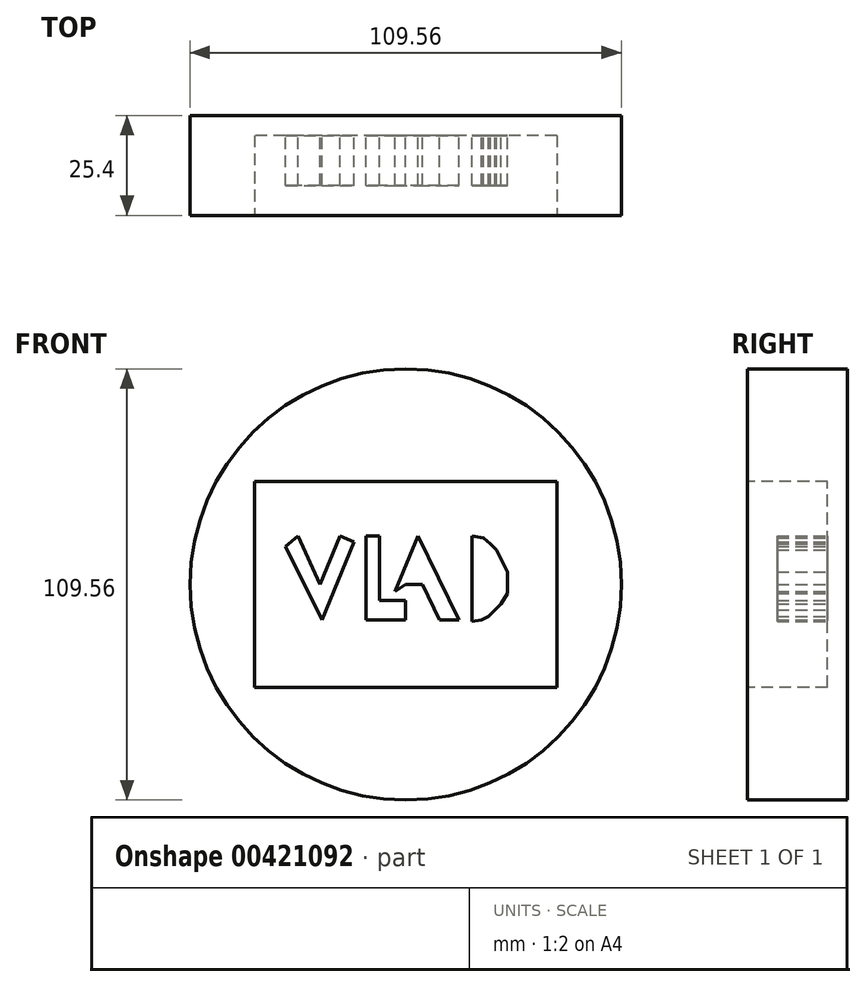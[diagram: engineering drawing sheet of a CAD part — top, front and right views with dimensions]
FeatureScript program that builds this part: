
annotation { "Feature Type Name" : "Feature", "Feature Type Description" : "" }
export const myFeature = defineFeature(function(context is Context, id is Id, definition is map)
    precondition{}
    {
        {
            var Q0;
            Q0=qCreatedBy(makeId("Front.planeOp"),FACE);
            var sketch = newSketch(context, id + "F0", { "sketchPlane" : qUnion([Q0])});
            skCircle(sketch, "E0", {"center": v(0, 0) * mm, "radius": 54.78 * mm});
            skSolve(sketch);
        }
        {
            var Q0;
            Q0 = qSketchRegion(id + "F0", true);
            extrude(context, id + "F1", {"entities" : qUnion([Q0]), "depth" : 25.4 * mm});
        }
        {
            var Q0;
            Q0=makeQuery(id+"F1.opExtrude","CAP_FACE",FACE,{"disambiguationData":[OSD([sQuery(id+"F0.wireOp",EDGE,"E0")])],"isStart":false});
            var sketch = newSketch(context, id + "F2", { "sketchPlane" : qUnion([Q0])});
            skLineSegment(sketch, "E1.bottom", {"start": v(38.38, -26.15) * mm, "end": v(-38.38, -26.15) * mm});
            skLineSegment(sketch, "E1.top", {"start": v(38.38, 26.15) * mm, "end": v(-38.38, 26.15) * mm});
            skLineSegment(sketch, "E1.left", {"start": v(38.38, -26.15) * mm, "end": v(38.38, 26.15) * mm});
            skLineSegment(sketch, "E1.right", {"start": v(-38.38, -26.15) * mm, "end": v(-38.38, 26.15) * mm});
            skPoint(sketch, "E1.middle", {"position": v(0, 0) * mm});
            skSolve(sketch);
        }
        {
            var Q0;
            Q0=makeQuery(id+"F2.imprint","IMPRINT",FACE,{"disambiguationData":[TD([[makeQuery(id+"F2.imprint","IMPRINT",EDGE,{"derivedFrom":sQuery(id+"F2.wireOp",EDGE,"E1.bottom")}),-1.0]])]});
            extrude(context, id + "F3", {"entities" : qUnion([Q0]), "operationType" : NewBodyOperationType.REMOVE, "oppositeDirection" : true, "depth" : 20.32 * mm});
        }
        {
            var Q0;
            Q0=makeQuery(id+"F3.boolean.opBoolean","COPY",FACE,{"derivedFrom":makeQuery(id+"F3.opExtrude","CAP_FACE",FACE,{"disambiguationData":[OSD([sQuery(id+"F2.wireOp",EDGE,"E1.bottom"),sQuery(id+"F2.wireOp",EDGE,"E1.top"),sQuery(id+"F2.wireOp",EDGE,"E1.left"),sQuery(id+"F2.wireOp",EDGE,"E1.right")])],"isStart":false})});
            var sketch = newSketch(context, id + "F4", { "sketchPlane" : qUnion([Q0])});
            skLineSegment(sketch, "E2", {"start": v(-30.48, 9.68) * mm, "end": v(-21.32, -8.96) * mm});
            skLineSegment(sketch, "E3", {"start": v(-21.32, -8.96) * mm, "end": v(-13.15, 10.82) * mm});
            skLineSegment(sketch, "E4", {"start": v(-13.15, 10.82) * mm, "end": v(-16.73, 12.3) * mm});
            skLineSegment(sketch, "E5", {"start": v(-16.73, 12.3) * mm, "end": v(-21.81, 0) * mm});
            skLineSegment(sketch, "E6", {"start": v(-21.81, 0) * mm, "end": v(-27.37, 12.3) * mm});
            skLineSegment(sketch, "E7", {"start": v(-27.37, 12.3) * mm, "end": v(-30.48, 9.68) * mm});
            skLineSegment(sketch, "E8", {"start": v(-10.04, 12.3) * mm, "end": v(-10.04, -8.96) * mm});
            skLineSegment(sketch, "E9", {"start": v(-10.04, -8.96) * mm, "end": v(0, -8.96) * mm});
            skLineSegment(sketch, "E10", {"start": v(0, -8.96) * mm, "end": v(0, -4.06) * mm});
            skLineSegment(sketch, "E11", {"start": v(0, -4.06) * mm, "end": v(-6.6, -4.06) * mm});
            skLineSegment(sketch, "E12", {"start": v(-6.6, -4.06) * mm, "end": v(-6.6, 12.3) * mm});
            skLineSegment(sketch, "E13", {"start": v(-6.6, 12.3) * mm, "end": v(-10.04, 12.3) * mm});
            skLineSegment(sketch, "E14", {"start": v(-2.68, -1.77) * mm, "end": v(3.13, 12.3) * mm});
            skLineSegment(sketch, "E15", {"start": v(3.13, 12.3) * mm, "end": v(13.58, -8.96) * mm});
            skLineSegment(sketch, "E16", {"start": v(13.58, -8.96) * mm, "end": v(8.6, -8.96) * mm});
            skLineSegment(sketch, "E17", {"start": v(8.6, -8.96) * mm, "end": v(4.2, 0) * mm});
            skLineSegment(sketch, "E18", {"start": v(4.2, 0) * mm, "end": v(0, 0) * mm});
            skLineSegment(sketch, "E19", {"start": v(0, 0) * mm, "end": v(-2.68, -1.77) * mm});
            skLineSegment(sketch, "E20", {"start": v(1.24, 2.48) * mm, "end": v(3.01, 6.77) * mm});
            skLineSegment(sketch, "E21", {"start": v(3.01, 6.77) * mm, "end": v(5.1, 2.53) * mm});
            skLineSegment(sketch, "E22", {"start": v(5.1, 2.53) * mm, "end": v(1.24, 2.48) * mm});
            skLineSegment(sketch, "E23", {"start": v(16.84, 12.3) * mm, "end": v(16.84, -9.44) * mm});
            skLineSegment(sketch, "E24", {"start": v(16.84, -9.44) * mm, "end": v(19.2, -8.96) * mm});
            skLineSegment(sketch, "E25", {"start": v(19.2, -8.96) * mm, "end": v(21.04, -8.05) * mm});
            skLineSegment(sketch, "E26", {"start": v(21.04, -8.05) * mm, "end": v(22.67, -6.43) * mm});
            skLineSegment(sketch, "E27", {"start": v(22.67, -6.43) * mm, "end": v(24.2, -4.96) * mm});
            skLineSegment(sketch, "E28", {"start": v(24.2, -4.96) * mm, "end": v(25.8, -2.25) * mm});
            skLineSegment(sketch, "E29", {"start": v(25.8, -2.25) * mm, "end": v(25.8, 0.7) * mm});
            skLineSegment(sketch, "E30", {"start": v(25.8, 0.7) * mm, "end": v(25.8, 3.23) * mm});
            skLineSegment(sketch, "E31", {"start": v(25.8, 3.23) * mm, "end": v(25.12, 4.6) * mm});
            skLineSegment(sketch, "E32", {"start": v(25.12, 4.6) * mm, "end": v(24.21, 6.45) * mm});
            skLineSegment(sketch, "E33", {"start": v(24.21, 6.45) * mm, "end": v(23.08, 8.77) * mm});
            skLineSegment(sketch, "E34", {"start": v(23.08, 8.77) * mm, "end": v(21.55, 10.24) * mm});
            skLineSegment(sketch, "E35", {"start": v(21.55, 10.24) * mm, "end": v(19.78, 11.78) * mm});
            skLineSegment(sketch, "E36", {"start": v(19.78, 11.78) * mm, "end": v(16.84, 12.3) * mm});
            skLineSegment(sketch, "E37", {"start": v(18.66, 6.41) * mm, "end": v(19.2, -4.84) * mm});
            skLineSegment(sketch, "E38", {"start": v(19.2, -4.84) * mm, "end": v(23.26, 0.64) * mm});
            skLineSegment(sketch, "E39", {"start": v(23.26, 0.64) * mm, "end": v(18.66, 6.41) * mm});
            skSolve(sketch);
        }
        {
            var Q0;
            Q0=makeQuery(id+"F4.imprint","IMPRINT",FACE,{"disambiguationData":[TD([[makeQuery(id+"F4.imprint","IMPRINT",EDGE,{"derivedFrom":sQuery(id+"F4.wireOp",EDGE,"E23")}),1.0]])]});
            var Q1;
            Q1=makeQuery(id+"F4.imprint","IMPRINT",FACE,{"disambiguationData":[TD([[makeQuery(id+"F4.imprint","IMPRINT",EDGE,{"derivedFrom":sQuery(id+"F4.wireOp",EDGE,"E14")}),-1.0]])]});
            var Q2;
            Q2=makeQuery(id+"F4.imprint","IMPRINT",FACE,{"disambiguationData":[TD([[makeQuery(id+"F4.imprint","IMPRINT",EDGE,{"derivedFrom":sQuery(id+"F4.wireOp",EDGE,"E37")}),1.0]])]});
            var Q3;
            Q3=makeQuery(id+"F4.imprint","IMPRINT",FACE,{"disambiguationData":[TD([[makeQuery(id+"F4.imprint","IMPRINT",EDGE,{"derivedFrom":sQuery(id+"F4.wireOp",EDGE,"E2")}),1.0]])]});
            var Q4;
            Q4=makeQuery(id+"F4.imprint","IMPRINT",FACE,{"disambiguationData":[TD([[makeQuery(id+"F4.imprint","IMPRINT",EDGE,{"derivedFrom":sQuery(id+"F4.wireOp",EDGE,"E8")}),1.0]])]});
            var Q5;
            Q5=makeQuery(id+"F4.imprint","IMPRINT",FACE,{"disambiguationData":[TD([[makeQuery(id+"F4.imprint","IMPRINT",EDGE,{"derivedFrom":sQuery(id+"F4.wireOp",EDGE,"E20")}),-1.0]])]});
            extrude(context, id + "F5", {"entities" : qUnion([Q0, Q1, Q2, Q3, Q4, Q5]), "operationType" : NewBodyOperationType.ADD, "depth" : 12.7 * mm});
        }
    });
